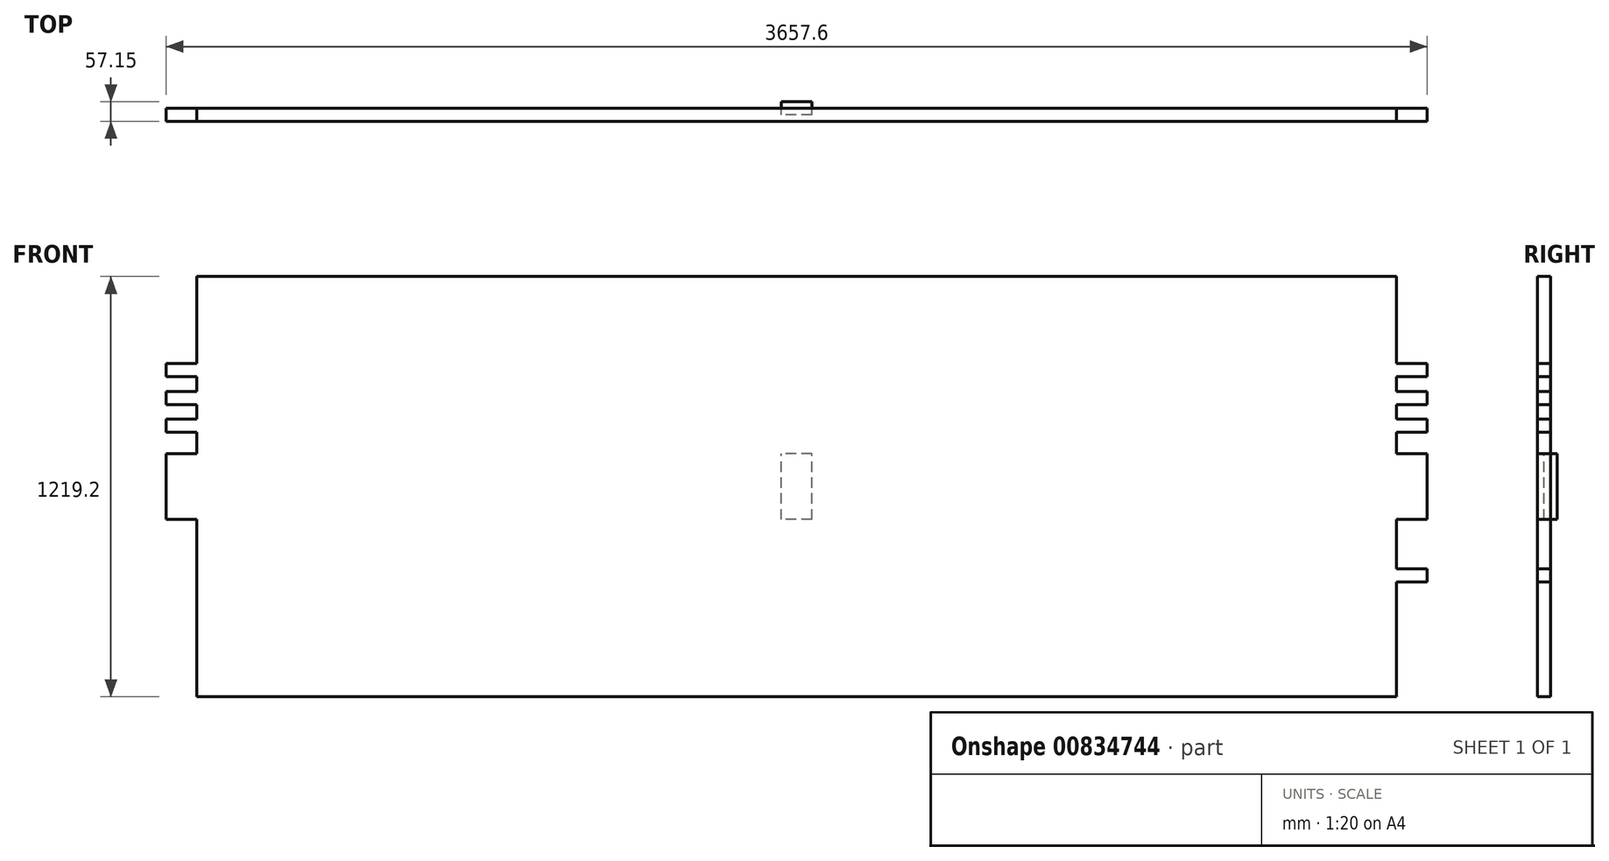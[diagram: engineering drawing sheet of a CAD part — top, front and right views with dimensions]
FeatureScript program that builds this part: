
annotation { "Feature Type Name" : "Feature", "Feature Type Description" : "" }
export const myFeature = defineFeature(function(context is Context, id is Id, definition is map)
    precondition{}
    {
        {
            var Q0;
            Q0=qCreatedBy(makeId("Front.planeOp"),FACE);
            var sketch = newSketch(context, id + "F0", { "sketchPlane" : qUnion([Q0])});
            skLineSegment(sketch, "E0.bottom", {"start": v(1828.8, -609.6) * mm, "end": v(-1828.8, -609.6) * mm});
            skLineSegment(sketch, "E0.top", {"start": v(1828.8, 609.6) * mm, "end": v(-1828.8, 609.6) * mm});
            skLineSegment(sketch, "E0.left", {"start": v(1828.8, -609.6) * mm, "end": v(1828.8, 609.6) * mm});
            skLineSegment(sketch, "E0.right", {"start": v(-1828.8, -609.6) * mm, "end": v(-1828.8, 609.6) * mm});
            skPoint(sketch, "E0.middle", {"position": v(0, 0) * mm});
            skLineSegment(sketch, "E1.bottom", {"start": v(1828.8, -95.25) * mm, "end": v(-1828.8, -95.25) * mm});
            skLineSegment(sketch, "E1.top", {"start": v(1828.8, 95.25) * mm, "end": v(-1828.8, 95.25) * mm});
            skLineSegment(sketch, "E1.left", {"start": v(1828.8, -95.25) * mm, "end": v(1828.8, 95.25) * mm});
            skLineSegment(sketch, "E1.right", {"start": v(-1828.8, -95.25) * mm, "end": v(-1828.8, 95.25) * mm});
            skLineSegment(sketch, "E2.bottom", {"start": v(-1828.8, -609.6) * mm, "end": v(1828.8, -609.6) * mm});
            skLineSegment(sketch, "E2.top", {"start": v(-1828.8, -419.1) * mm, "end": v(1828.8, -419.1) * mm});
            skLineSegment(sketch, "E2.left", {"start": v(-1828.8, -609.6) * mm, "end": v(-1828.8, -419.1) * mm});
            skLineSegment(sketch, "E2.right", {"start": v(1828.8, -609.6) * mm, "end": v(1828.8, -419.1) * mm});
            skLineSegment(sketch, "E3.top", {"start": v(-1828.8, -95.25) * mm, "end": v(1828.8, -95.25) * mm});
            skLineSegment(sketch, "E3.left", {"start": v(-1828.8, -419.1) * mm, "end": v(-1828.8, -95.25) * mm});
            skLineSegment(sketch, "E3.right", {"start": v(1828.8, -419.1) * mm, "end": v(1828.8, -95.25) * mm});
            skLineSegment(sketch, "E4.bottom", {"start": v(1828.8, -276.23) * mm, "end": v(-1828.8, -276.23) * mm});
            skLineSegment(sketch, "E4.top", {"start": v(1828.8, -238.12) * mm, "end": v(-1828.8, -238.12) * mm});
            skLineSegment(sketch, "E4.left", {"start": v(1828.8, -276.23) * mm, "end": v(1828.8, -238.12) * mm});
            skLineSegment(sketch, "E4.right", {"start": v(-1828.8, -276.23) * mm, "end": v(-1828.8, -238.12) * mm});
            skPoint(sketch, "E4.middle", {"position": v(0, -257.18) * mm});
            skPoint(sketch, "E4.middle.positionSnap0", {"position": v(-1828.8, -257.18) * mm});
            skPoint(sketch, "E4.centerSnap0", {"position": v(-1828.8, -257.18) * mm});
            skLineSegment(sketch, "E5.MirrorCS", {"start": v(-1828.8, 276.23) * mm, "end": v(-1828.8, 238.12) * mm});
            skLineSegment(sketch, "E6.MirrorCS", {"start": v(-1828.8, 419.1) * mm, "end": v(-1828.8, 95.25) * mm});
            skLineSegment(sketch, "E7.MirrorCS", {"start": v(1828.8, 276.23) * mm, "end": v(1828.8, 238.12) * mm});
            skLineSegment(sketch, "E8.MirrorCS", {"start": v(1828.8, 419.1) * mm, "end": v(1828.8, 95.25) * mm});
            skPoint(sketch, "E9.MirrorP", {"position": v(-1828.8, 257.18) * mm});
            skLineSegment(sketch, "E10.MirrorCS", {"start": v(-1828.8, 609.6) * mm, "end": v(-1828.8, -609.6) * mm});
            skLineSegment(sketch, "E11.MirrorCS", {"start": v(1828.8, 609.6) * mm, "end": v(1828.8, -609.6) * mm});
            skLineSegment(sketch, "E12.MirrorCS", {"start": v(-1828.8, 419.1) * mm, "end": v(1828.8, 419.1) * mm});
            skLineSegment(sketch, "E13.MirrorCS", {"start": v(1828.8, 238.12) * mm, "end": v(-1828.8, 238.12) * mm});
            skLineSegment(sketch, "E14.MirrorCS", {"start": v(-1828.8, 609.6) * mm, "end": v(-1828.8, 419.1) * mm});
            skLineSegment(sketch, "E15.MirrorCS", {"start": v(1828.8, 276.23) * mm, "end": v(-1828.8, 276.23) * mm});
            skLineSegment(sketch, "E16.MirrorCS", {"start": v(1828.8, 609.6) * mm, "end": v(1828.8, 419.1) * mm});
            skPoint(sketch, "E17.MirrorP", {"position": v(0, 257.18) * mm});
            skLineSegment(sketch, "E18.MirrorCS", {"start": v(-1828.8, 95.25) * mm, "end": v(1828.8, 95.25) * mm});
            skLineSegment(sketch, "E19.MirrorCS", {"start": v(-1828.8, 609.6) * mm, "end": v(1828.8, 609.6) * mm});
            skLineSegment(sketch, "E20.MirrorCS", {"start": v(-1828.8, 95.25) * mm, "end": v(-1828.8, -95.25) * mm});
            skLineSegment(sketch, "E21.MirrorCS", {"start": v(1828.8, 95.25) * mm, "end": v(1828.8, -95.25) * mm});
            skLineSegment(sketch, "E22.bottom", {"start": v(-1828.8, 609.6) * mm, "end": v(-1739.9, 609.6) * mm});
            skLineSegment(sketch, "E22.top", {"start": v(-1828.8, -609.6) * mm, "end": v(-1739.9, -609.6) * mm});
            skLineSegment(sketch, "E22.right", {"start": v(-1739.9, 609.6) * mm, "end": v(-1739.9, -609.6) * mm});
            skLineSegment(sketch, "E23.MirrorCS", {"start": v(1828.8, -609.6) * mm, "end": v(1739.9, -609.6) * mm});
            skLineSegment(sketch, "E24.MirrorCS", {"start": v(1828.8, 609.6) * mm, "end": v(1739.9, 609.6) * mm});
            skPoint(sketch, "E25.MirrorP", {"position": v(1828.8, 257.18) * mm});
            skPoint(sketch, "E26.MirrorP", {"position": v(1828.8, -257.18) * mm});
            skLineSegment(sketch, "E27.MirrorCS", {"start": v(1739.9, 609.6) * mm, "end": v(1739.9, -609.6) * mm});
            skLineSegment(sketch, "E28.bottom", {"start": v(44.45, -609.6) * mm, "end": v(-44.45, -609.6) * mm});
            skLineSegment(sketch, "E28.top", {"start": v(44.45, 609.6) * mm, "end": v(-44.45, 609.6) * mm});
            skLineSegment(sketch, "E28.left", {"start": v(44.45, -609.6) * mm, "end": v(44.45, 609.6) * mm});
            skLineSegment(sketch, "E28.right", {"start": v(-44.45, -609.6) * mm, "end": v(-44.45, 609.6) * mm});
            skLineSegment(sketch, "E29", {"start": v(-1828.8, -257.18) * mm, "end": v(-1828.8, -419.1) * mm});
            skLineSegment(sketch, "E30.bottom", {"start": v(-1828.8, -357.19) * mm, "end": v(1828.8, -357.19) * mm});
            skLineSegment(sketch, "E30.top", {"start": v(-1828.8, -319.09) * mm, "end": v(1828.8, -319.09) * mm});
            skLineSegment(sketch, "E30.left", {"start": v(-1828.8, -357.19) * mm, "end": v(-1828.8, -319.09) * mm});
            skLineSegment(sketch, "E30.right", {"start": v(1828.8, -357.19) * mm, "end": v(1828.8, -319.09) * mm});
            skPoint(sketch, "E30.middle", {"position": v(0, -338.14) * mm});
            skPoint(sketch, "E30.middle.positionSnap0", {"position": v(-1828.8, -338.14) * mm});
            skPoint(sketch, "E30.centerSnap0", {"position": v(-1828.8, -338.14) * mm});
            skLineSegment(sketch, "E31", {"start": v(0, -257.18) * mm, "end": v(14.17, -257.18) * mm});
            skLineSegment(sketch, "E32.MirrorCS", {"start": v(-1828.8, -157.16) * mm, "end": v(-1828.8, -195.26) * mm});
            skLineSegment(sketch, "E33.MirrorCS", {"start": v(1828.8, -157.16) * mm, "end": v(1828.8, -195.26) * mm});
            skPoint(sketch, "E34.MirrorP", {"position": v(-1828.8, -176.21) * mm});
            skPoint(sketch, "E35.MirrorP", {"position": v(0, -176.21) * mm});
            skLineSegment(sketch, "E36.MirrorCS", {"start": v(-1828.8, -157.16) * mm, "end": v(1828.8, -157.16) * mm});
            skLineSegment(sketch, "E37.MirrorCS", {"start": v(-1828.8, -195.26) * mm, "end": v(1828.8, -195.26) * mm});
            skLineSegment(sketch, "E38.MirrorCS", {"start": v(-1828.8, 157.16) * mm, "end": v(-1828.8, 195.26) * mm});
            skLineSegment(sketch, "E39.MirrorCS", {"start": v(-1828.8, 257.18) * mm, "end": v(-1828.8, 419.1) * mm});
            skLineSegment(sketch, "E40.MirrorCS", {"start": v(-1828.8, 357.19) * mm, "end": v(-1828.8, 319.09) * mm});
            skLineSegment(sketch, "E41.MirrorCS", {"start": v(1828.8, 157.16) * mm, "end": v(1828.8, 195.26) * mm});
            skLineSegment(sketch, "E42.MirrorCS", {"start": v(1828.8, 357.19) * mm, "end": v(1828.8, 319.09) * mm});
            skLineSegment(sketch, "E43.MirrorCS", {"start": v(0, 257.18) * mm, "end": v(14.17, 257.18) * mm});
            skPoint(sketch, "E44.MirrorP", {"position": v(-1828.8, 176.21) * mm});
            skPoint(sketch, "E45.MirrorP", {"position": v(-1828.8, 338.14) * mm});
            skLineSegment(sketch, "E46.MirrorCS", {"start": v(-1828.8, 157.16) * mm, "end": v(1828.8, 157.16) * mm});
            skLineSegment(sketch, "E47.MirrorCS", {"start": v(-1828.8, 319.09) * mm, "end": v(1828.8, 319.09) * mm});
            skLineSegment(sketch, "E48.MirrorCS", {"start": v(-1828.8, 195.26) * mm, "end": v(1828.8, 195.26) * mm});
            skPoint(sketch, "E49.MirrorP", {"position": v(0, 176.21) * mm});
            skPoint(sketch, "E50.MirrorP", {"position": v(0, 338.14) * mm});
            skLineSegment(sketch, "E51.MirrorCS", {"start": v(-1828.8, 357.19) * mm, "end": v(1828.8, 357.19) * mm});
            skSolve(sketch);
        }
        {
            var Q0;
            {var subQ0=sQuery(id+"F0.wireOp",EDGE,"E19.MirrorCS");var subQ1=sQuery(id+"F0.wireOp",EDGE,"E22.right");var subQ2=makeQuery(id+"F0.imprint","INTERSECT",VERTEX,{"derivedFrom":[subQ1,subQ0]});Q0=makeQuery(id+"F0.imprint","IMPRINT",FACE,{"disambiguationData":[TD([[makeQuery(id+"F0.imprint","IMPRINT",EDGE,{"disambiguationData":[TD([[subQ2,-1.0]])],"derivedFrom":subQ1}),1.0]])]});}
            var Q1;
            {var subQ0=sQuery(id+"F0.wireOp",EDGE,"E19.MirrorCS");var subQ1=sQuery(id+"F0.wireOp",EDGE,"E28.left");var subQ2=makeQuery(id+"F0.imprint","INTERSECT",VERTEX,{"derivedFrom":[subQ1,subQ0]});Q1=makeQuery(id+"F0.imprint","IMPRINT",FACE,{"disambiguationData":[TD([[makeQuery(id+"F0.imprint","IMPRINT",EDGE,{"disambiguationData":[TD([[subQ2,1.0]])],"derivedFrom":subQ1}),1.0]])]});}
            var Q2;
            {var subQ0=sQuery(id+"F0.wireOp",EDGE,"E19.MirrorCS");var subQ1=sQuery(id+"F0.wireOp",EDGE,"E27.MirrorCS");var subQ2=makeQuery(id+"F0.imprint","INTERSECT",VERTEX,{"derivedFrom":[subQ1,subQ0]});Q2=makeQuery(id+"F0.imprint","IMPRINT",FACE,{"disambiguationData":[TD([[makeQuery(id+"F0.imprint","IMPRINT",EDGE,{"disambiguationData":[TD([[subQ2,-1.0]])],"derivedFrom":subQ1}),-1.0]])]});}
            var Q3;
            {var subQ5=sQuery(id+"F0.wireOp",EDGE,"E16.MirrorCS");Q3=makeQuery(id+"F0.imprint","IMPRINT",FACE,{"disambiguationData":[TD([[makeQuery(id+"F0.imprint","IMPRINT",EDGE,{"derivedFrom":subQ5}),-1.0]])]});}
            var Q4;
            {var subQ5=sQuery(id+"F0.wireOp",EDGE,"E14.MirrorCS");Q4=makeQuery(id+"F0.imprint","IMPRINT",FACE,{"disambiguationData":[TD([[makeQuery(id+"F0.imprint","IMPRINT",EDGE,{"derivedFrom":subQ5}),1.0]])]});}
            var Q5;
            {var subQ0=sQuery(id+"F0.wireOp",EDGE,"E28.right");var subQ1=sQuery(id+"F0.wireOp",EDGE,"E1.bottom");var subQ2=makeQuery(id+"F0.imprint","INTERSECT",VERTEX,{"derivedFrom":[subQ1,subQ0]});Q5=makeQuery(id+"F0.imprint","IMPRINT",FACE,{"disambiguationData":[TD([[makeQuery(id+"F0.imprint","IMPRINT",EDGE,{"disambiguationData":[TD([[subQ2,-1.0]])],"derivedFrom":subQ1}),-1.0]])]});}
            var Q6;
            {var subQ0=sQuery(id+"F0.wireOp",EDGE,"E28.left");var subQ1=sQuery(id+"F0.wireOp",EDGE,"E1.bottom");var subQ2=makeQuery(id+"F0.imprint","INTERSECT",VERTEX,{"derivedFrom":[subQ1,subQ0]});Q6=makeQuery(id+"F0.imprint","IMPRINT",FACE,{"disambiguationData":[TD([[makeQuery(id+"F0.imprint","IMPRINT",EDGE,{"disambiguationData":[TD([[subQ2,-1.0]])],"derivedFrom":subQ1}),-1.0]])]});}
            var Q7;
            {var subQ0=sQuery(id+"F0.wireOp",EDGE,"E27.MirrorCS");var subQ1=sQuery(id+"F0.wireOp",EDGE,"E1.bottom");var subQ2=makeQuery(id+"F0.imprint","INTERSECT",VERTEX,{"derivedFrom":[subQ1,subQ0]});Q7=makeQuery(id+"F0.imprint","IMPRINT",FACE,{"disambiguationData":[TD([[makeQuery(id+"F0.imprint","IMPRINT",EDGE,{"disambiguationData":[TD([[subQ2,-1.0]])],"derivedFrom":subQ1}),-1.0]])]});}
            var Q8;
            {var subQ0=sQuery(id+"F0.wireOp",EDGE,"E1.left");Q8=makeQuery(id+"F0.imprint","IMPRINT",FACE,{"disambiguationData":[TD([[makeQuery(id+"F0.imprint","IMPRINT",EDGE,{"derivedFrom":subQ0}),1.0]])]});}
            var Q9;
            {var subQ0=sQuery(id+"F0.wireOp",EDGE,"E10.MirrorCS");var subQ1=sQuery(id+"F0.wireOp",EDGE,"E1.bottom");var subQ2=makeQuery(id+"F0.imprint","INTERSECT",VERTEX,{"derivedFrom":[subQ1,subQ0]});Q9=makeQuery(id+"F0.imprint","IMPRINT",FACE,{"disambiguationData":[TD([[makeQuery(id+"F0.imprint","IMPRINT",EDGE,{"disambiguationData":[TD([[subQ2,1.0]])],"derivedFrom":subQ1}),-1.0]])]});}
            var Q10;
            {var subQ5=sQuery(id+"F0.wireOp",EDGE,"E30.left");Q10=makeQuery(id+"F0.imprint","IMPRINT",FACE,{"disambiguationData":[TD([[makeQuery(id+"F0.imprint","IMPRINT",EDGE,{"derivedFrom":subQ5}),-1.0]])]});}
            var Q11;
            {var subQ0=sQuery(id+"F0.wireOp",EDGE,"E30.top");var subQ1=sQuery(id+"F0.wireOp",EDGE,"E22.right");var subQ2=makeQuery(id+"F0.imprint","INTERSECT",VERTEX,{"derivedFrom":[subQ1,subQ0]});Q11=makeQuery(id+"F0.imprint","IMPRINT",FACE,{"disambiguationData":[TD([[makeQuery(id+"F0.imprint","IMPRINT",EDGE,{"disambiguationData":[TD([[subQ2,-1.0]])],"derivedFrom":subQ1}),1.0]])]});}
            var Q12;
            {var subQ0=sQuery(id+"F0.wireOp",EDGE,"E30.top");var subQ1=sQuery(id+"F0.wireOp",EDGE,"E27.MirrorCS");var subQ2=makeQuery(id+"F0.imprint","INTERSECT",VERTEX,{"derivedFrom":[subQ1,subQ0]});Q12=makeQuery(id+"F0.imprint","IMPRINT",FACE,{"disambiguationData":[TD([[makeQuery(id+"F0.imprint","IMPRINT",EDGE,{"disambiguationData":[TD([[subQ2,-1.0]])],"derivedFrom":subQ1}),-1.0]])]});}
            var Q13;
            {var subQ0=sQuery(id+"F0.wireOp",EDGE,"E30.bottom");var subQ1=sQuery(id+"F0.wireOp",EDGE,"E28.left");var subQ2=makeQuery(id+"F0.imprint","INTERSECT",VERTEX,{"derivedFrom":[subQ1,subQ0]});Q13=makeQuery(id+"F0.imprint","IMPRINT",FACE,{"disambiguationData":[TD([[makeQuery(id+"F0.imprint","IMPRINT",EDGE,{"disambiguationData":[TD([[subQ2,-1.0]])],"derivedFrom":subQ1}),1.0]])]});}
            var Q14;
            {var subQ5=sQuery(id+"F0.wireOp",EDGE,"E30.right");Q14=makeQuery(id+"F0.imprint","IMPRINT",FACE,{"disambiguationData":[TD([[makeQuery(id+"F0.imprint","IMPRINT",EDGE,{"derivedFrom":subQ5}),1.0]])]});}
            var Q15;
            {var subQ4=sQuery(id+"F0.wireOp",EDGE,"E23.MirrorCS");Q15=makeQuery(id+"F0.imprint","IMPRINT",FACE,{"disambiguationData":[TD([[makeQuery(id+"F0.imprint","IMPRINT",EDGE,{"derivedFrom":subQ4}),-1.0]])]});}
            var Q16;
            {var subQ3=sQuery(id+"F0.wireOp",EDGE,"E28.left");var subQ5=sQuery(id+"F0.wireOp",EDGE,"E2.top");var subQ6=makeQuery(id+"F0.imprint","INTERSECT",VERTEX,{"derivedFrom":[subQ5,subQ3]});Q16=makeQuery(id+"F0.imprint","IMPRINT",FACE,{"disambiguationData":[TD([[makeQuery(id+"F0.imprint","IMPRINT",EDGE,{"disambiguationData":[TD([[subQ6,-1.0]])],"derivedFrom":subQ5}),-1.0]])]});}
            var Q17;
            {var subQ5=sQuery(id+"F0.wireOp",EDGE,"E28.bottom");Q17=makeQuery(id+"F0.imprint","IMPRINT",FACE,{"disambiguationData":[TD([[makeQuery(id+"F0.imprint","IMPRINT",EDGE,{"derivedFrom":subQ5}),-1.0]])]});}
            var Q18;
            {var subQ0=sQuery(id+"F0.wireOp",EDGE,"E22.right");var subQ5=sQuery(id+"F0.wireOp",EDGE,"E2.top");var subQ6=makeQuery(id+"F0.imprint","INTERSECT",VERTEX,{"derivedFrom":[subQ5,subQ0]});Q18=makeQuery(id+"F0.imprint","IMPRINT",FACE,{"disambiguationData":[TD([[makeQuery(id+"F0.imprint","IMPRINT",EDGE,{"disambiguationData":[TD([[subQ6,-1.0]])],"derivedFrom":subQ5}),-1.0]])]});}
            var Q19;
            {var subQ5=sQuery(id+"F0.wireOp",EDGE,"E22.top");Q19=makeQuery(id+"F0.imprint","IMPRINT",FACE,{"disambiguationData":[TD([[makeQuery(id+"F0.imprint","IMPRINT",EDGE,{"derivedFrom":subQ5}),1.0]])]});}
            var Q20;
            {var subQ0=sQuery(id+"F0.wireOp",EDGE,"E51.MirrorCS");var subQ1=sQuery(id+"F0.wireOp",EDGE,"E22.right");var subQ2=makeQuery(id+"F0.imprint","INTERSECT",VERTEX,{"derivedFrom":[subQ1,subQ0]});Q20=makeQuery(id+"F0.imprint","IMPRINT",FACE,{"disambiguationData":[TD([[makeQuery(id+"F0.imprint","IMPRINT",EDGE,{"disambiguationData":[TD([[subQ2,-1.0]])],"derivedFrom":subQ1}),-1.0]])]});}
            var Q21;
            {var subQ0=sQuery(id+"F0.wireOp",EDGE,"E51.MirrorCS");var subQ1=sQuery(id+"F0.wireOp",EDGE,"E22.right");var subQ2=makeQuery(id+"F0.imprint","INTERSECT",VERTEX,{"derivedFrom":[subQ1,subQ0]});Q21=makeQuery(id+"F0.imprint","IMPRINT",FACE,{"disambiguationData":[TD([[makeQuery(id+"F0.imprint","IMPRINT",EDGE,{"disambiguationData":[TD([[subQ2,-1.0]])],"derivedFrom":subQ1}),1.0]])]});}
            var Q22;
            {var subQ0=sQuery(id+"F0.wireOp",EDGE,"E47.MirrorCS");var subQ1=sQuery(id+"F0.wireOp",EDGE,"E28.left");var subQ2=makeQuery(id+"F0.imprint","INTERSECT",VERTEX,{"derivedFrom":[subQ1,subQ0]});Q22=makeQuery(id+"F0.imprint","IMPRINT",FACE,{"disambiguationData":[TD([[makeQuery(id+"F0.imprint","IMPRINT",EDGE,{"disambiguationData":[TD([[subQ2,-1.0]])],"derivedFrom":subQ1}),1.0]])]});}
            var Q23;
            {var subQ0=sQuery(id+"F0.wireOp",EDGE,"E51.MirrorCS");var subQ1=sQuery(id+"F0.wireOp",EDGE,"E27.MirrorCS");var subQ2=makeQuery(id+"F0.imprint","INTERSECT",VERTEX,{"derivedFrom":[subQ1,subQ0]});Q23=makeQuery(id+"F0.imprint","IMPRINT",FACE,{"disambiguationData":[TD([[makeQuery(id+"F0.imprint","IMPRINT",EDGE,{"disambiguationData":[TD([[subQ2,-1.0]])],"derivedFrom":subQ1}),1.0]])]});}
            var Q24;
            {var subQ0=sQuery(id+"F0.wireOp",EDGE,"E51.MirrorCS");var subQ1=sQuery(id+"F0.wireOp",EDGE,"E27.MirrorCS");var subQ2=makeQuery(id+"F0.imprint","INTERSECT",VERTEX,{"derivedFrom":[subQ1,subQ0]});Q24=makeQuery(id+"F0.imprint","IMPRINT",FACE,{"disambiguationData":[TD([[makeQuery(id+"F0.imprint","IMPRINT",EDGE,{"disambiguationData":[TD([[subQ2,-1.0]])],"derivedFrom":subQ1}),-1.0]])]});}
            var Q25;
            {var subQ0=sQuery(id+"F0.wireOp",EDGE,"E48.MirrorCS");var subQ1=sQuery(id+"F0.wireOp",EDGE,"E27.MirrorCS");var subQ2=makeQuery(id+"F0.imprint","INTERSECT",VERTEX,{"derivedFrom":[subQ1,subQ0]});Q25=makeQuery(id+"F0.imprint","IMPRINT",FACE,{"disambiguationData":[TD([[makeQuery(id+"F0.imprint","IMPRINT",EDGE,{"disambiguationData":[TD([[subQ2,-1.0]])],"derivedFrom":subQ1}),1.0]])]});}
            var Q26;
            {var subQ0=sQuery(id+"F0.wireOp",EDGE,"E48.MirrorCS");var subQ1=sQuery(id+"F0.wireOp",EDGE,"E27.MirrorCS");var subQ2=makeQuery(id+"F0.imprint","INTERSECT",VERTEX,{"derivedFrom":[subQ1,subQ0]});Q26=makeQuery(id+"F0.imprint","IMPRINT",FACE,{"disambiguationData":[TD([[makeQuery(id+"F0.imprint","IMPRINT",EDGE,{"disambiguationData":[TD([[subQ2,-1.0]])],"derivedFrom":subQ1}),-1.0]])]});}
            var Q27;
            {var subQ0=sQuery(id+"F0.wireOp",EDGE,"E46.MirrorCS");var subQ1=sQuery(id+"F0.wireOp",EDGE,"E28.left");var subQ2=makeQuery(id+"F0.imprint","INTERSECT",VERTEX,{"derivedFrom":[subQ1,subQ0]});Q27=makeQuery(id+"F0.imprint","IMPRINT",FACE,{"disambiguationData":[TD([[makeQuery(id+"F0.imprint","IMPRINT",EDGE,{"disambiguationData":[TD([[subQ2,-1.0]])],"derivedFrom":subQ1}),1.0]])]});}
            var Q28;
            {var subQ0=sQuery(id+"F0.wireOp",EDGE,"E48.MirrorCS");var subQ1=sQuery(id+"F0.wireOp",EDGE,"E22.right");var subQ2=makeQuery(id+"F0.imprint","INTERSECT",VERTEX,{"derivedFrom":[subQ1,subQ0]});Q28=makeQuery(id+"F0.imprint","IMPRINT",FACE,{"disambiguationData":[TD([[makeQuery(id+"F0.imprint","IMPRINT",EDGE,{"disambiguationData":[TD([[subQ2,-1.0]])],"derivedFrom":subQ1}),1.0]])]});}
            var Q29;
            {var subQ0=sQuery(id+"F0.wireOp",EDGE,"E48.MirrorCS");var subQ1=sQuery(id+"F0.wireOp",EDGE,"E22.right");var subQ2=makeQuery(id+"F0.imprint","INTERSECT",VERTEX,{"derivedFrom":[subQ1,subQ0]});Q29=makeQuery(id+"F0.imprint","IMPRINT",FACE,{"disambiguationData":[TD([[makeQuery(id+"F0.imprint","IMPRINT",EDGE,{"disambiguationData":[TD([[subQ2,-1.0]])],"derivedFrom":subQ1}),-1.0]])]});}
            var Q30;
            {var subQ0=sQuery(id+"F0.wireOp",EDGE,"E36.MirrorCS");var subQ1=sQuery(id+"F0.wireOp",EDGE,"E22.right");var subQ2=makeQuery(id+"F0.imprint","INTERSECT",VERTEX,{"derivedFrom":[subQ1,subQ0]});Q30=makeQuery(id+"F0.imprint","IMPRINT",FACE,{"disambiguationData":[TD([[makeQuery(id+"F0.imprint","IMPRINT",EDGE,{"disambiguationData":[TD([[subQ2,-1.0]])],"derivedFrom":subQ1}),1.0]])]});}
            var Q31;
            {var subQ5=sQuery(id+"F0.wireOp",EDGE,"E32.MirrorCS");Q31=makeQuery(id+"F0.imprint","IMPRINT",FACE,{"disambiguationData":[TD([[makeQuery(id+"F0.imprint","IMPRINT",EDGE,{"derivedFrom":subQ5}),1.0]])]});}
            var Q32;
            {var subQ0=sQuery(id+"F0.wireOp",EDGE,"E37.MirrorCS");var subQ1=sQuery(id+"F0.wireOp",EDGE,"E28.left");var subQ2=makeQuery(id+"F0.imprint","INTERSECT",VERTEX,{"derivedFrom":[subQ1,subQ0]});Q32=makeQuery(id+"F0.imprint","IMPRINT",FACE,{"disambiguationData":[TD([[makeQuery(id+"F0.imprint","IMPRINT",EDGE,{"disambiguationData":[TD([[subQ2,-1.0]])],"derivedFrom":subQ1}),1.0]])]});}
            var Q33;
            {var subQ0=sQuery(id+"F0.wireOp",EDGE,"E36.MirrorCS");var subQ1=sQuery(id+"F0.wireOp",EDGE,"E27.MirrorCS");var subQ2=makeQuery(id+"F0.imprint","INTERSECT",VERTEX,{"derivedFrom":[subQ1,subQ0]});Q33=makeQuery(id+"F0.imprint","IMPRINT",FACE,{"disambiguationData":[TD([[makeQuery(id+"F0.imprint","IMPRINT",EDGE,{"disambiguationData":[TD([[subQ2,-1.0]])],"derivedFrom":subQ1}),-1.0]])]});}
            var Q34;
            {var subQ5=sQuery(id+"F0.wireOp",EDGE,"E33.MirrorCS");Q34=makeQuery(id+"F0.imprint","IMPRINT",FACE,{"disambiguationData":[TD([[makeQuery(id+"F0.imprint","IMPRINT",EDGE,{"derivedFrom":subQ5}),-1.0]])]});}
            var Q35;
            {var subQ0=sQuery(id+"F0.wireOp",EDGE,"E0.left");var subQ1=sQuery(id+"F0.wireOp",EDGE,"E4.bottom");var subQ2=makeQuery(id+"F0.imprint","INTERSECT",VERTEX,{"derivedFrom":[subQ1,subQ0]});Q35=makeQuery(id+"F0.imprint","IMPRINT",FACE,{"disambiguationData":[TD([[makeQuery(id+"F0.imprint","IMPRINT",EDGE,{"disambiguationData":[TD([[subQ2,-1.0]])],"derivedFrom":subQ1}),-1.0]])]});}
            var Q36;
            {var subQ0=sQuery(id+"F0.wireOp",EDGE,"E27.MirrorCS");var subQ1=sQuery(id+"F0.wireOp",EDGE,"E4.bottom");var subQ2=makeQuery(id+"F0.imprint","INTERSECT",VERTEX,{"derivedFrom":[subQ1,subQ0]});Q36=makeQuery(id+"F0.imprint","IMPRINT",FACE,{"disambiguationData":[TD([[makeQuery(id+"F0.imprint","IMPRINT",EDGE,{"disambiguationData":[TD([[subQ2,-1.0]])],"derivedFrom":subQ1}),-1.0]])]});}
            var Q37;
            {var subQ0=sQuery(id+"F0.wireOp",EDGE,"E28.left");var subQ1=sQuery(id+"F0.wireOp",EDGE,"E4.bottom");var subQ2=makeQuery(id+"F0.imprint","INTERSECT",VERTEX,{"derivedFrom":[subQ1,subQ0]});Q37=makeQuery(id+"F0.imprint","IMPRINT",FACE,{"disambiguationData":[TD([[makeQuery(id+"F0.imprint","IMPRINT",EDGE,{"disambiguationData":[TD([[subQ2,-1.0]])],"derivedFrom":subQ1}),-1.0]])]});}
            var Q38;
            {var subQ0=sQuery(id+"F0.wireOp",EDGE,"E28.right");var subQ1=sQuery(id+"F0.wireOp",EDGE,"E4.bottom");var subQ2=makeQuery(id+"F0.imprint","INTERSECT",VERTEX,{"derivedFrom":[subQ1,subQ0]});Q38=makeQuery(id+"F0.imprint","IMPRINT",FACE,{"disambiguationData":[TD([[makeQuery(id+"F0.imprint","IMPRINT",EDGE,{"disambiguationData":[TD([[subQ2,-1.0]])],"derivedFrom":subQ1}),-1.0]])]});}
            var Q39;
            {var subQ1=sQuery(id+"F0.wireOp",EDGE,"E4.bottom");var subQ7=sQuery(id+"F0.wireOp",EDGE,"E29");var subQ9=makeQuery(id+"F0.imprint","INTERSECT",VERTEX,{"derivedFrom":[subQ1,subQ7]});Q39=makeQuery(id+"F0.imprint","IMPRINT",FACE,{"disambiguationData":[TD([[makeQuery(id+"F0.imprint","IMPRINT",EDGE,{"disambiguationData":[TD([[subQ9,1.0]])],"derivedFrom":subQ1}),-1.0]])]});}
            var Q40;
            {var subQ0=sQuery(id+"F0.wireOp",EDGE,"E15.MirrorCS");var subQ1=sQuery(id+"F0.wireOp",EDGE,"E27.MirrorCS");var subQ2=makeQuery(id+"F0.imprint","INTERSECT",VERTEX,{"derivedFrom":[subQ1,subQ0]});Q40=makeQuery(id+"F0.imprint","IMPRINT",FACE,{"disambiguationData":[TD([[makeQuery(id+"F0.imprint","IMPRINT",EDGE,{"disambiguationData":[TD([[subQ2,-1.0]])],"derivedFrom":subQ1}),1.0]])]});}
            var Q41;
            {var subQ0=sQuery(id+"F0.wireOp",EDGE,"E15.MirrorCS");var subQ1=sQuery(id+"F0.wireOp",EDGE,"E27.MirrorCS");var subQ2=makeQuery(id+"F0.imprint","INTERSECT",VERTEX,{"derivedFrom":[subQ1,subQ0]});Q41=makeQuery(id+"F0.imprint","IMPRINT",FACE,{"disambiguationData":[TD([[makeQuery(id+"F0.imprint","IMPRINT",EDGE,{"disambiguationData":[TD([[subQ2,-1.0]])],"derivedFrom":subQ1}),-1.0]])]});}
            var Q42;
            {var subQ0=sQuery(id+"F0.wireOp",EDGE,"E13.MirrorCS");var subQ1=sQuery(id+"F0.wireOp",EDGE,"E28.left");var subQ2=makeQuery(id+"F0.imprint","INTERSECT",VERTEX,{"derivedFrom":[subQ1,subQ0]});Q42=makeQuery(id+"F0.imprint","IMPRINT",FACE,{"disambiguationData":[TD([[makeQuery(id+"F0.imprint","IMPRINT",EDGE,{"disambiguationData":[TD([[subQ2,-1.0]])],"derivedFrom":subQ1}),1.0]])]});}
            var Q43;
            {var subQ0=sQuery(id+"F0.wireOp",EDGE,"E15.MirrorCS");var subQ1=sQuery(id+"F0.wireOp",EDGE,"E22.right");var subQ2=makeQuery(id+"F0.imprint","INTERSECT",VERTEX,{"derivedFrom":[subQ1,subQ0]});Q43=makeQuery(id+"F0.imprint","IMPRINT",FACE,{"disambiguationData":[TD([[makeQuery(id+"F0.imprint","IMPRINT",EDGE,{"disambiguationData":[TD([[subQ2,-1.0]])],"derivedFrom":subQ1}),1.0]])]});}
            var Q44;
            {var subQ0=sQuery(id+"F0.wireOp",EDGE,"E15.MirrorCS");var subQ1=sQuery(id+"F0.wireOp",EDGE,"E22.right");var subQ2=makeQuery(id+"F0.imprint","INTERSECT",VERTEX,{"derivedFrom":[subQ1,subQ0]});Q44=makeQuery(id+"F0.imprint","IMPRINT",FACE,{"disambiguationData":[TD([[makeQuery(id+"F0.imprint","IMPRINT",EDGE,{"disambiguationData":[TD([[subQ2,-1.0]])],"derivedFrom":subQ1}),-1.0]])]});}
            extrude(context, id + "F1", {"entities" : qUnion([Q0, Q1, Q2, Q3, Q4, Q5, Q6, Q7, Q8, Q9, Q10, Q11, Q12, Q13, Q14, Q15, Q16, Q17, Q18, Q19, Q20, Q21, Q22, Q23, Q24, Q25, Q26, Q27, Q28, Q29, Q30, Q31, Q32, Q33, Q34, Q35, Q36, Q37, Q38, Q39, Q40, Q41, Q42, Q43, Q44]), "depth" : 38.1 * mm, "offsetDistance" : 25.4 * mm});
        }
        {
            var Q0;
            {var subQ0=sQuery(id+"F0.wireOp",EDGE,"E28.left");var subQ1=sQuery(id+"F0.wireOp",EDGE,"E1.bottom");var subQ2=makeQuery(id+"F0.imprint","INTERSECT",VERTEX,{"derivedFrom":[subQ1,subQ0]});Q0=makeQuery(id+"F0.imprint","IMPRINT",FACE,{"disambiguationData":[TD([[makeQuery(id+"F0.imprint","IMPRINT",EDGE,{"disambiguationData":[TD([[subQ2,-1.0]])],"derivedFrom":subQ1}),-1.0]])]});}
            var sketch = newSketch(context, id + "F2", { "sketchPlane" : qUnion([Q0])});
            skLineSegment(sketch, "E52.bottom", {"start": v(-1828.8, -609.6) * mm, "end": v(1828.8, -609.6) * mm});
            skLineSegment(sketch, "E52.top", {"start": v(-1828.8, 609.6) * mm, "end": v(1828.8, 609.6) * mm});
            skLineSegment(sketch, "E52.left", {"start": v(-1828.8, -609.6) * mm, "end": v(-1828.8, 609.6) * mm});
            skLineSegment(sketch, "E52.right", {"start": v(1828.8, -609.6) * mm, "end": v(1828.8, 609.6) * mm});
            skPoint(sketch, "E52.middle", {"position": v(0, 0) * mm});
            skLineSegment(sketch, "E53.bottom", {"start": v(-1828.8, 609.6) * mm, "end": v(-1739.9, 609.6) * mm});
            skLineSegment(sketch, "E53.top", {"start": v(-1828.8, -609.6) * mm, "end": v(-1739.9, -609.6) * mm});
            skLineSegment(sketch, "E53.left", {"start": v(-1828.8, 609.6) * mm, "end": v(-1828.8, -609.6) * mm});
            skLineSegment(sketch, "E53.right", {"start": v(-1739.9, 609.6) * mm, "end": v(-1739.9, -609.6) * mm});
            skLineSegment(sketch, "E54.MirrorCS", {"start": v(1828.8, 609.6) * mm, "end": v(1739.9, 609.6) * mm});
            skLineSegment(sketch, "E55.MirrorCS", {"start": v(1828.8, -609.6) * mm, "end": v(1739.9, -609.6) * mm});
            skLineSegment(sketch, "E56.MirrorCS", {"start": v(1828.8, 609.6) * mm, "end": v(1828.8, -609.6) * mm});
            skLineSegment(sketch, "E57.MirrorCS", {"start": v(1739.9, 609.6) * mm, "end": v(1739.9, -609.6) * mm});
            skLineSegment(sketch, "E58.bottom", {"start": v(-44.45, -609.6) * mm, "end": v(44.45, -609.6) * mm});
            skLineSegment(sketch, "E58.top", {"start": v(-44.45, 609.6) * mm, "end": v(44.45, 609.6) * mm});
            skLineSegment(sketch, "E58.left", {"start": v(-44.45, -609.6) * mm, "end": v(-44.45, 609.6) * mm});
            skLineSegment(sketch, "E58.right", {"start": v(44.45, -609.6) * mm, "end": v(44.45, 609.6) * mm});
            skSolve(sketch);
        }
        {
            var Q0;
            Q0=makeQuery(id+"F2.imprint","IMPRINT",FACE,{"disambiguationData":[TD([[makeQuery(id+"F2.imprint","IMPRINT",EDGE,{"derivedFrom":sQuery(id+"F2.wireOp",EDGE,"E53.bottom")}),-1.0]])]});
            var Q1;
            Q1=makeQuery(id+"F2.imprint","IMPRINT",FACE,{"disambiguationData":[TD([[makeQuery(id+"F2.imprint","IMPRINT",EDGE,{"derivedFrom":sQuery(id+"F2.wireOp",EDGE,"E54.MirrorCS")}),1.0]])]});
            var Q2;
            {var subQ0=sQuery(id+"F2.wireOp",EDGE,"E58.bottom");Q2=makeQuery(id+"F2.imprint","IMPRINT",FACE,{"disambiguationData":[TD([[makeQuery(id+"F2.imprint","IMPRINT",EDGE,{"derivedFrom":subQ0}),1.0]])]});}
            var Q3;
            {var subQ0=sQuery(id+"F2.wireOp",EDGE,"E58.top");Q3=makeQuery(id+"F2.imprint","IMPRINT",FACE,{"disambiguationData":[TD([[makeQuery(id+"F2.imprint","IMPRINT",EDGE,{"derivedFrom":subQ0}),-1.0]])]});}
            var Q4;
            {var subQ1=sQuery(id+"F0.wireOp",EDGE,"E28.left");var subQ2=sQuery(id+"F0.wireOp",EDGE,"E1.bottom");var subQ4=makeQuery(id+"F0.imprint","IMPRINT",EDGE,{"disambiguationData":[TD([[makeQuery(id+"F0.imprint","INTERSECT",VERTEX,{"derivedFrom":[subQ2,subQ1]}),-1.0]])],"derivedFrom":subQ2});Q4=makeQuery(id+"F2.imprint","IMPRINT",FACE,{"disambiguationData":[TD([[makeQuery(id+"F2.imprint","IMPRINT",EDGE,{"derivedFrom":subQ4}),-1.0]])]});}
            extrude(context, id + "F3", {"entities" : qUnion([Q0, Q1, Q2, Q3, Q4]), "endBound" : BoundingType.SYMMETRIC, "depth" : 38.1 * mm, "offsetDistance" : 25.4 * mm});
        }
    });
